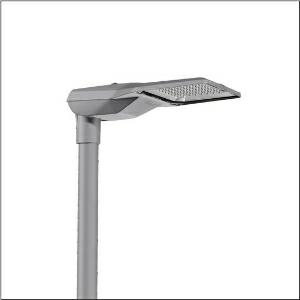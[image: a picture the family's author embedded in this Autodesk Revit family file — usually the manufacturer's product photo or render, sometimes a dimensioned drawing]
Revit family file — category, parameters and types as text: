
# Revit family: streetlight_sl_21_midi___st1_0ab_5xe3m33s08mb_fd22
name_source: partatom
category: Lighting Fixtures
units: mm (PartAtom-declared; Revit-internal decimal feet)

## family parameters
Cut with Voids When Loaded = No
Host = Face
Light Source = No
Part Type = Normal
Room Calculation Point = No
Round Connector Dimension = Use Diameter
Shared = No

## types (1)
- --- (1 x LED, 16080 lm, 136 W, 3000K)
    Apparent Load = 136 VA
    CIE Flux Codes = 38 73 97 100 100
    Color Rendering = 70
    Color Temperature = 3000K
    Default Elevation = 1800 mm
    Description = Streetlight SL 21 midi, mast luminaire, primary light control with lens, of PMMA, primary optical cover: cover, of toughened safety glass, transparent, light distribution: ST1.0aB, light emission: direct distribution, primary light characteristic: asymmetric, installation type: side-entry, post-top, LED, High Power LED, rated luminous flux: 16.080lm, luminous efficacy: 118lm/W, light colour: 730, colour temperature: 3000K, control gear: D4i, control: flexible luminous flux parameterisation, time-dependent luminous flux control, constant luminous flux control, overheat protection, pre-setting: logarithmic dimming characteristic, mains connection: 230..240V, AC, 50/60Hz, start of lifetime: 136W, end of service life: 142W, reduction: 61W, luminaire housing, of diecast aluminium, powder-coated, Siteco® metallic grey (DB 702S), corrosivity category C5 mid according to DIN EN ISO 12944, please order mast flange separately, inclination adjustable: 0°, 5°, 10°, 15°, sealing non-destructively replaceable, multi-level sealing system, length: 644mm, width: 335mm, height: 110mm, mast flange for spigot size: 42mm (side-entry): 5XC10008XM4, 60/48mm (side-entry/post-top): 5XC10108XM2, 76/60mm (side-entry/post-top): 5XC10108XM1, mounting height: 4..8m, Smart Interface above, protection rating (complete): IP66, insulation class (complete): insulation class II (safety insulation), certification: CE, ENEC, ENEC+, VDE, impact resistance: IK10, permissible operating ambient temperature for outdoor applications: -40..+50°C, standard-compliant lighting for roads and squares, packaging unit: 1 piece

Light Distribution: ST1.0aB
    Height = 111 mm
    Lamp = 1 x LED
    Lamp Light Flux = 16080 lm
    Lamp Power = 136 W
    Lamp count = 1
    Length = 644 mm
    Luminous efficacy = 118 lm/W
    Manufacturer = Siteco
    ModVariant = No
    Model = 5XE3M33S08MB
    Number of Poles = 1
    OnlyDefault = Yes
    Power Factor = 1
    Product Name = Streetlight SL 21 midi | ST1.0aB
    Product group = mast luminaire | pylon top
    ProductGroupID = 6100
    Protection Class = Protection class II
    Protection Degree = IP 66
    RLX_Detail_Level = 1
    RLX_Emergency_Light_Flux = 0 lm
    RLX_Emergency_Type = 0
    RLX_Emergency_Type_DB = No
    RlxData = <blob elided: 26897 chars, md5=b253a741>
    Socket = socket
    Standby Power = 0 W
    System Light Flux = 16081 lm
    System Power = 136 W
    Type Comments = factory setting: luminous flux: 100 % | dim-lin: 254 | 695 mA
    Type Image = l_1004302.jpg
    URL = http://relux.com
    VarID = @adj_204221
    Voltage = 0 V
    Weight = 0.00 kg
    Width = 336 mm

## geometry (parser evidence)
native form markers: Blend x4, Sweep x11
no freeform markers — native parametric forms only
